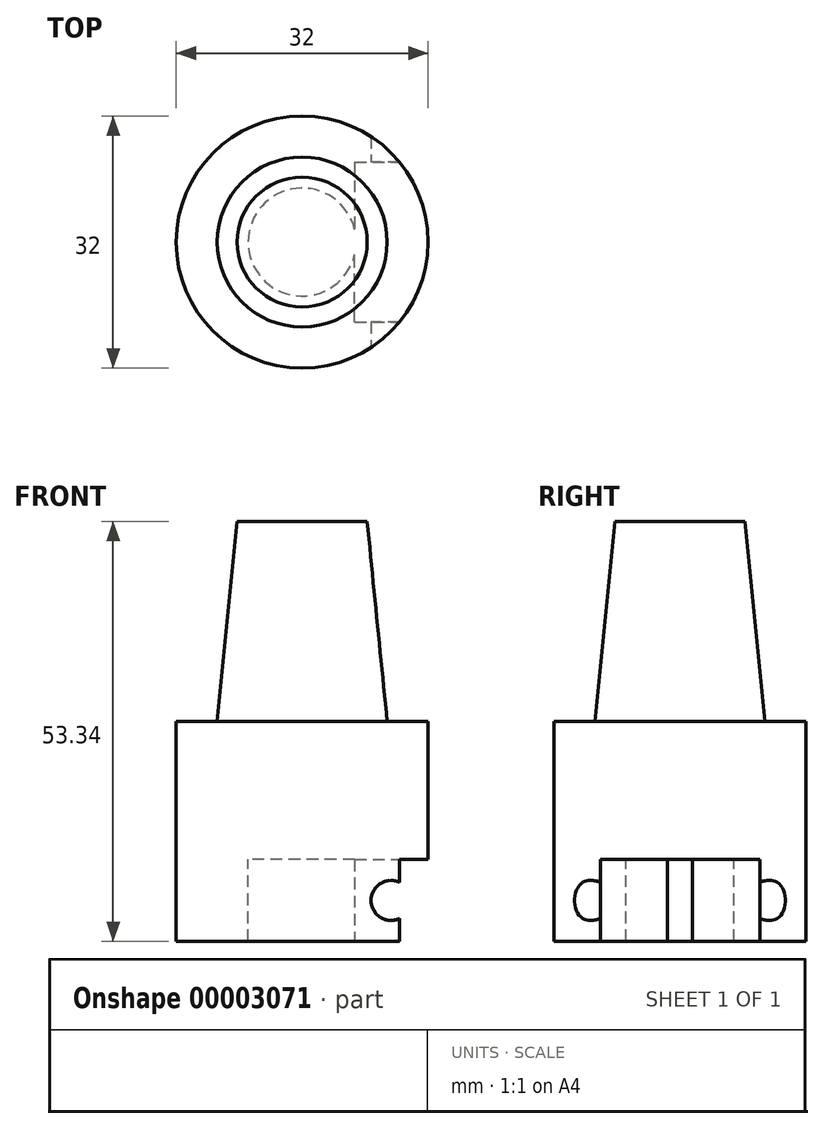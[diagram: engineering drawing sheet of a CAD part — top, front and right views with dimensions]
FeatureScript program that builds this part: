
annotation { "Feature Type Name" : "Feature", "Feature Type Description" : "" }
export const myFeature = defineFeature(function(context is Context, id is Id, definition is map)
    precondition{}
    {
        {
            var Q0;
            Q0=qCreatedBy(makeId("Front.planeOp"),FACE);
            var sketch = newSketch(context, id + "F0", { "sketchPlane" : qUnion([Q0])});
            skLineSegment(sketch, "E0", {"start": v(0, 23.94) * mm, "end": v(0, -31.16) * mm, "construction": true});
            skLineSegment(sketch, "E1", {"start": v(0, 23.94) * mm, "end": v(8.26, 23.94) * mm});
            skLineSegment(sketch, "E2", {"start": v(8.25, 23.94) * mm, "end": v(10.8, -1.46) * mm});
            skLineSegment(sketch, "E3", {"start": v(10.8, -1.46) * mm, "end": v(16, -1.46) * mm});
            skLineSegment(sketch, "E4", {"start": v(16, -1.46) * mm, "end": v(16, -29.4) * mm});
            skLineSegment(sketch, "E5", {"start": v(16, -29.4) * mm, "end": v(6.86, -29.4) * mm});
            skLineSegment(sketch, "E6", {"start": v(6.86, -29.4) * mm, "end": v(6.86, -18.99) * mm});
            skLineSegment(sketch, "E7", {"start": v(6.86, -18.99) * mm, "end": v(0, -18.99) * mm});
            skLineSegment(sketch, "E8", {"start": v(0, -18.99) * mm, "end": v(0, 23.94) * mm});
            skSolve(sketch);
        }
        {
            var Q0;
            Q0=makeQuery(id+"F0.imprint","IMPRINT",FACE,{"disambiguationData":[TD([[makeQuery(id+"F0.imprint","IMPRINT",EDGE,{"derivedFrom":sQuery(id+"F0.wireOp",EDGE,"E1")}),-1.0]])]});
            var Q1;
            Q1=sQuery(id+"F0.wireOp",EDGE,"E0");
            revolve(context, id + "F1", {"entities" : qUnion([Q0]), "axis" : qUnion([Q1]), "revolveType" : RevolveType.FULL});
        }
        {
            var Q0;
            Q0=makeQuery(id+"F1.opRevolve","SWEPT_FACE",FACE,{"disambiguationData":[OSD([sQuery(id+"F0.wireOp",EDGE,"E5")])]});
            var sketch = newSketch(context, id + "F2", { "sketchPlane" : qUnion([Q0])});
            skLineSegment(sketch, "E9.bottom", {"start": v(5.56, 1.59) * mm, "end": v(17.37, 1.59) * mm});
            skLineSegment(sketch, "E9.top", {"start": v(5.56, -1.59) * mm, "end": v(17.37, -1.59) * mm});
            skLineSegment(sketch, "E9.left", {"start": v(5.56, 1.59) * mm, "end": v(5.56, -1.59) * mm});
            skLineSegment(sketch, "E9.right", {"start": v(17.37, 1.59) * mm, "end": v(17.37, -1.59) * mm});
            skLineSegment(sketch, "E10", {"start": v(5.56, 0) * mm, "end": v(17.37, 0) * mm, "construction": true});
            skSolve(sketch);
        }
        {
            var Q0;
            {var subQ0=sQuery(id+"F0.wireOp",EDGE,"E5");var subQ4=sQuery(id+"F2.wireOp",EDGE,"E9.bottom");var subQ6=makeQuery(id+"F1.opRevolve","SWEPT_EDGE",EDGE,{"disambiguationData":[OSD([sQuery(id+"F0.wireOp",EDGE,"E4"),subQ0])]});var subQ8=makeQuery(id+"F2.imprint","INTERSECT",VERTEX,{"derivedFrom":[subQ6,subQ4]});Q0=makeQuery(id+"F2.imprint","IMPRINT",FACE,{"disambiguationData":[TD([[makeQuery(id+"F2.imprint","IMPRINT",EDGE,{"disambiguationData":[TD([[subQ8,1.0]])],"derivedFrom":subQ4}),-1.0]])]});}
            extrude(context, id + "F3", {"entities" : qUnion([Q0]), "operationType" : NewBodyOperationType.REMOVE, "oppositeDirection" : true, "depth" : 10.4 * mm});
        }
        {
            var Q0;
            Q0=qCreatedBy(makeId("Front.planeOp"),FACE);
            var sketch = newSketch(context, id + "F4", { "sketchPlane" : qUnion([Q0])});
            skLineSegment(sketch, "E11.0.0", {"start": v(6.67, -29.4) * mm, "end": v(15.92, -29.4) * mm});
            skLineSegment(sketch, "E11.0.1", {"start": v(6.67, -18.99) * mm, "end": v(6.67, -29.4) * mm});
            skLineSegment(sketch, "E11.0.2", {"start": v(6.67, -18.99) * mm, "end": v(15.92, -18.99) * mm});
            skLineSegment(sketch, "E11.0.3", {"start": v(15.92, -18.99) * mm, "end": v(15.92, -29.4) * mm});
            skLineSegment(sketch, "E12", {"start": v(11.3, -18.99) * mm, "end": v(11.3, -29.4) * mm, "construction": true});
            skLineSegment(sketch, "E13", {"start": v(15.92, -24.2) * mm, "end": v(6.67, -24.2) * mm, "construction": true});
            skCircle(sketch, "E14", {"center": v(11.3, -24.2) * mm, "radius": 2.54 * mm});
            skSolve(sketch);
        }
        {
            var Q0;
            Q0=makeQuery(id+"F4.imprint","IMPRINT",FACE,{"disambiguationData":[TD([[makeQuery(id+"F4.imprint","IMPRINT",EDGE,{"derivedFrom":sQuery(id+"F4.wireOp",EDGE,"E14")}),1.0]])]});
            extrude(context, id + "F5", {"entities" : qUnion([Q0]), "operationType" : NewBodyOperationType.REMOVE, "endBound" : BoundingType.SYMMETRIC, "oppositeDirection" : true, "depth" : 30.48 * mm});
        }
        {
            var Q0;
            Q0=qCreatedBy(makeId("Front.planeOp"),FACE);
            cPlane(context, id + "F6", {"entities" : qUnion([Q0]), "cplaneType" : CPlaneType.OFFSET, "offset" : 1.26 / 50.8 * mm, "width" : 152.4 * mm, "height" : 152.4 * mm});
        }
        {
            var Q0;
            Q0=qCreatedBy(id+"F6.planeOp",FACE);
            var sketch = newSketch(context, id + "F7", { "sketchPlane" : qUnion([Q0])});
            skLineSegment(sketch, "E15.0.0", {"start": v(6.67, -29.4) * mm, "end": v(15.92, -29.4) * mm});
            skLineSegment(sketch, "E15.0.1", {"start": v(15.92, -18.99) * mm, "end": v(15.92, -29.4) * mm});
            skLineSegment(sketch, "E15.0.2", {"start": v(6.67, -18.99) * mm, "end": v(15.92, -18.99) * mm});
            skLineSegment(sketch, "E15.0.3", {"start": v(6.67, -18.99) * mm, "end": v(6.67, -29.4) * mm});
            skSolve(sketch);
        }
        {
            var Q0;
            Q0=makeQuery(id+"F7.imprint","IMPRINT",FACE,{"disambiguationData":[TD([[makeQuery(id+"F7.imprint","IMPRINT",EDGE,{"derivedFrom":sQuery(id+"F7.wireOp",EDGE,"E15.0.0")}),1.0]])]});
            extrude(context, id + "F8", {"entities" : qUnion([Q0]), "operationType" : NewBodyOperationType.REMOVE, "oppositeDirection" : true, "depth" : 10.16 * mm});
        }
        {
            var Q0;
            Q0=qCreatedBy(makeId("Front.planeOp"),FACE);
            cPlane(context, id + "F9", {"entities" : qUnion([Q0]), "cplaneType" : CPlaneType.OFFSET, "offset" : 1.26 / 50.8 * mm, "oppositeDirection" : true, "width" : 152.4 * mm, "height" : 152.4 * mm});
        }
        {
            var Q0;
            Q0=qCreatedBy(id+"F9.planeOp",FACE);
            var sketch = newSketch(context, id + "F10", { "sketchPlane" : qUnion([Q0])});
            skLineSegment(sketch, "E16.0.0", {"start": v(6.67, -29.4) * mm, "end": v(15.92, -29.4) * mm});
            skLineSegment(sketch, "E16.0.1", {"start": v(15.92, -18.99) * mm, "end": v(15.92, -29.4) * mm});
            skLineSegment(sketch, "E16.0.2", {"start": v(6.67, -18.99) * mm, "end": v(15.92, -18.99) * mm});
            skLineSegment(sketch, "E16.0.3", {"start": v(6.67, -18.99) * mm, "end": v(6.67, -29.4) * mm});
            skSolve(sketch);
        }
        {
            var Q0;
            Q0=makeQuery(id+"F10.imprint","IMPRINT",FACE,{"disambiguationData":[TD([[makeQuery(id+"F10.imprint","IMPRINT",EDGE,{"derivedFrom":sQuery(id+"F10.wireOp",EDGE,"E16.0.0")}),1.0]])]});
            extrude(context, id + "F11", {"entities" : qUnion([Q0]), "operationType" : NewBodyOperationType.REMOVE, "depth" : 10.16 * mm});
        }
    });
